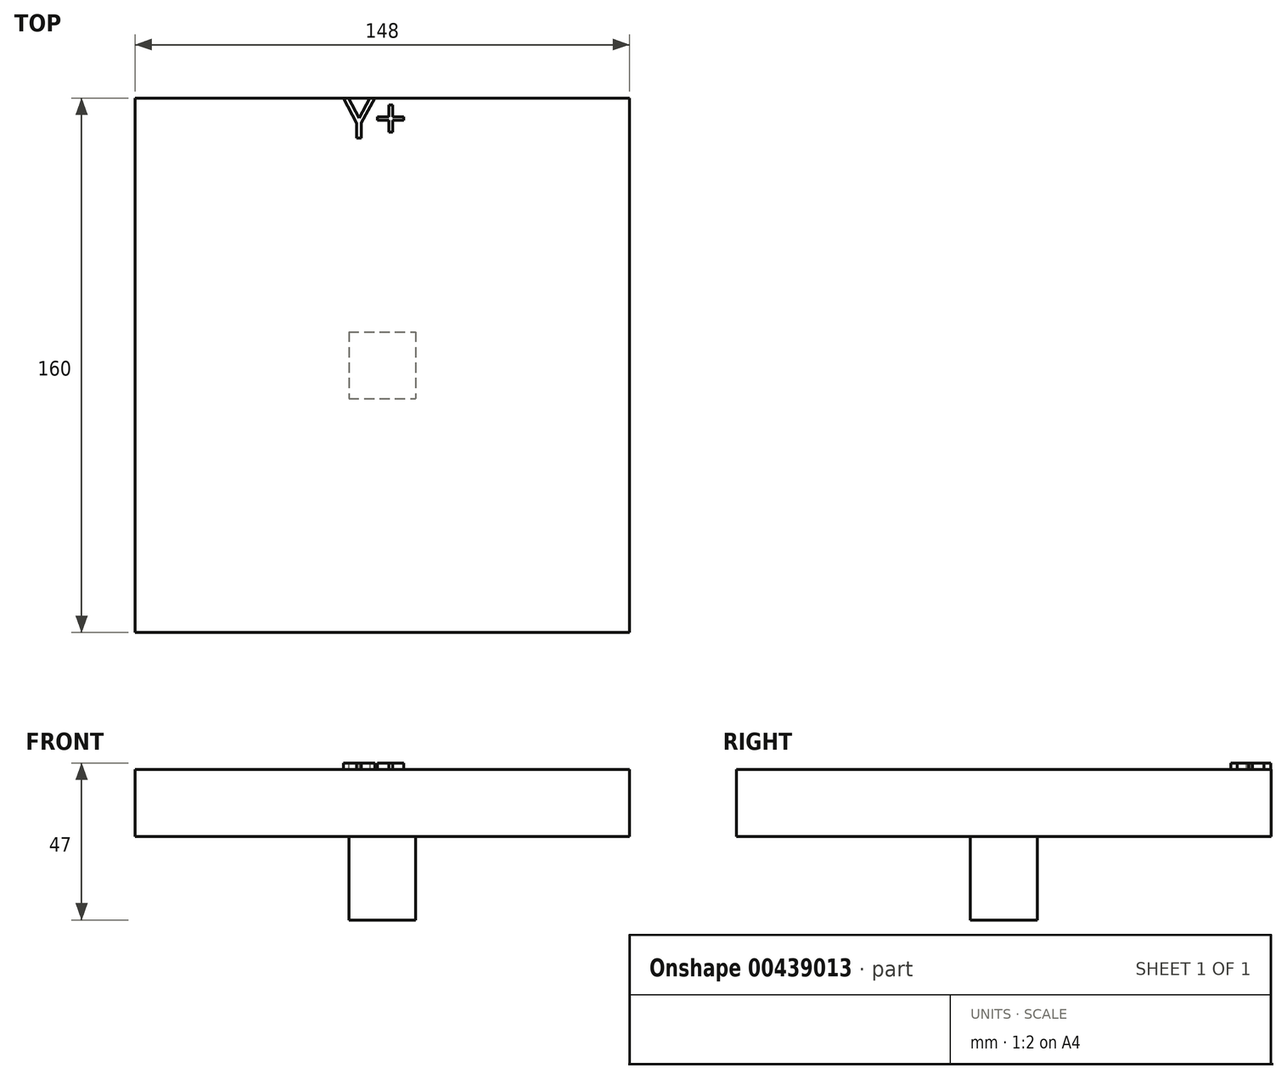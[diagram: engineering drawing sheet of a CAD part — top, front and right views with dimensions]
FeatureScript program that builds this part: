
annotation { "Feature Type Name" : "Feature", "Feature Type Description" : "" }
export const myFeature = defineFeature(function(context is Context, id is Id, definition is map)
    precondition{}
    {
        {
            var Q0;
            Q0=qCreatedBy(makeId("Top.planeOp"),FACE);
            var sketch = newSketch(context, id + "F0", { "sketchPlane" : qUnion([Q0])});
            skLineSegment(sketch, "E0.bottom", {"start": v(-4.26, 6.93) * mm, "end": v(15.74, 6.93) * mm});
            skLineSegment(sketch, "E0.top", {"start": v(-4.26, -13.07) * mm, "end": v(15.74, -13.07) * mm});
            skLineSegment(sketch, "E0.left", {"start": v(-4.26, 6.93) * mm, "end": v(-4.26, -13.07) * mm});
            skLineSegment(sketch, "E0.right", {"start": v(15.74, 6.93) * mm, "end": v(15.74, -13.07) * mm});
            skSolve(sketch);
        }
        {
            var Q0;
            Q0 = qSketchRegion(id + "F0", true);
            extrude(context, id + "F1", {"entities" : qUnion([Q0]), "depth" : 25 * mm});
        }
        {
            var Q0;
            Q0=makeQuery(id+"F1.opExtrude","CAP_FACE",FACE,{"disambiguationData":[OSD([sQuery(id+"F0.wireOp",EDGE,"E0.bottom"),sQuery(id+"F0.wireOp",EDGE,"E0.top"),sQuery(id+"F0.wireOp",EDGE,"E0.left"),sQuery(id+"F0.wireOp",EDGE,"E0.right")])],"isStart":false});
            var sketch = newSketch(context, id + "F2", { "sketchPlane" : qUnion([Q0])});
            skLineSegment(sketch, "E1.bottom", {"start": v(-68.26, 76.93) * mm, "end": v(79.74, 76.93) * mm});
            skLineSegment(sketch, "E1.top", {"start": v(-68.26, -83.07) * mm, "end": v(79.74, -83.07) * mm});
            skLineSegment(sketch, "E1.left", {"start": v(-68.26, 76.93) * mm, "end": v(-68.26, -83.07) * mm});
            skLineSegment(sketch, "E1.right", {"start": v(79.74, 76.93) * mm, "end": v(79.74, -83.07) * mm});
            skSolve(sketch);
        }
        {
            var Q0;
            Q0 = qSketchRegion(id + "F2", true);
            extrude(context, id + "F3", {"entities" : qUnion([Q0]), "operationType" : NewBodyOperationType.ADD, "depth" : 20 * mm});
        }
        {
            var Q0;
            Q0=makeQuery(id+"F3.opExtrude","CAP_FACE",FACE,{"disambiguationData":[OSD([sQuery(id+"F2.wireOp",EDGE,"E1.bottom"),sQuery(id+"F2.wireOp",EDGE,"E1.top"),sQuery(id+"F2.wireOp",EDGE,"E1.left"),sQuery(id+"F2.wireOp",EDGE,"E1.right")])],"isStart":false});
            var sketch = newSketch(context, id + "F4", { "sketchPlane" : qUnion([Q0])});
            skText(sketch, "E2", { "text": "Y+", "fontName": "OpenSans-Regular.ttf"});
            const initialGuessF4  = {"E2": [-0.0059, 0.06488, 1, 0, 0.01204]};
            skSetInitialGuess(sketch, initialGuessF4);
            skSolve(sketch);
        }
        {
            var Q0;
            Q0 = qSketchRegion(id + "F4", true);
            extrude(context, id + "F5", {"entities" : qUnion([Q0]), "operationType" : NewBodyOperationType.ADD, "depth" : 2 * mm});
        }
    });
